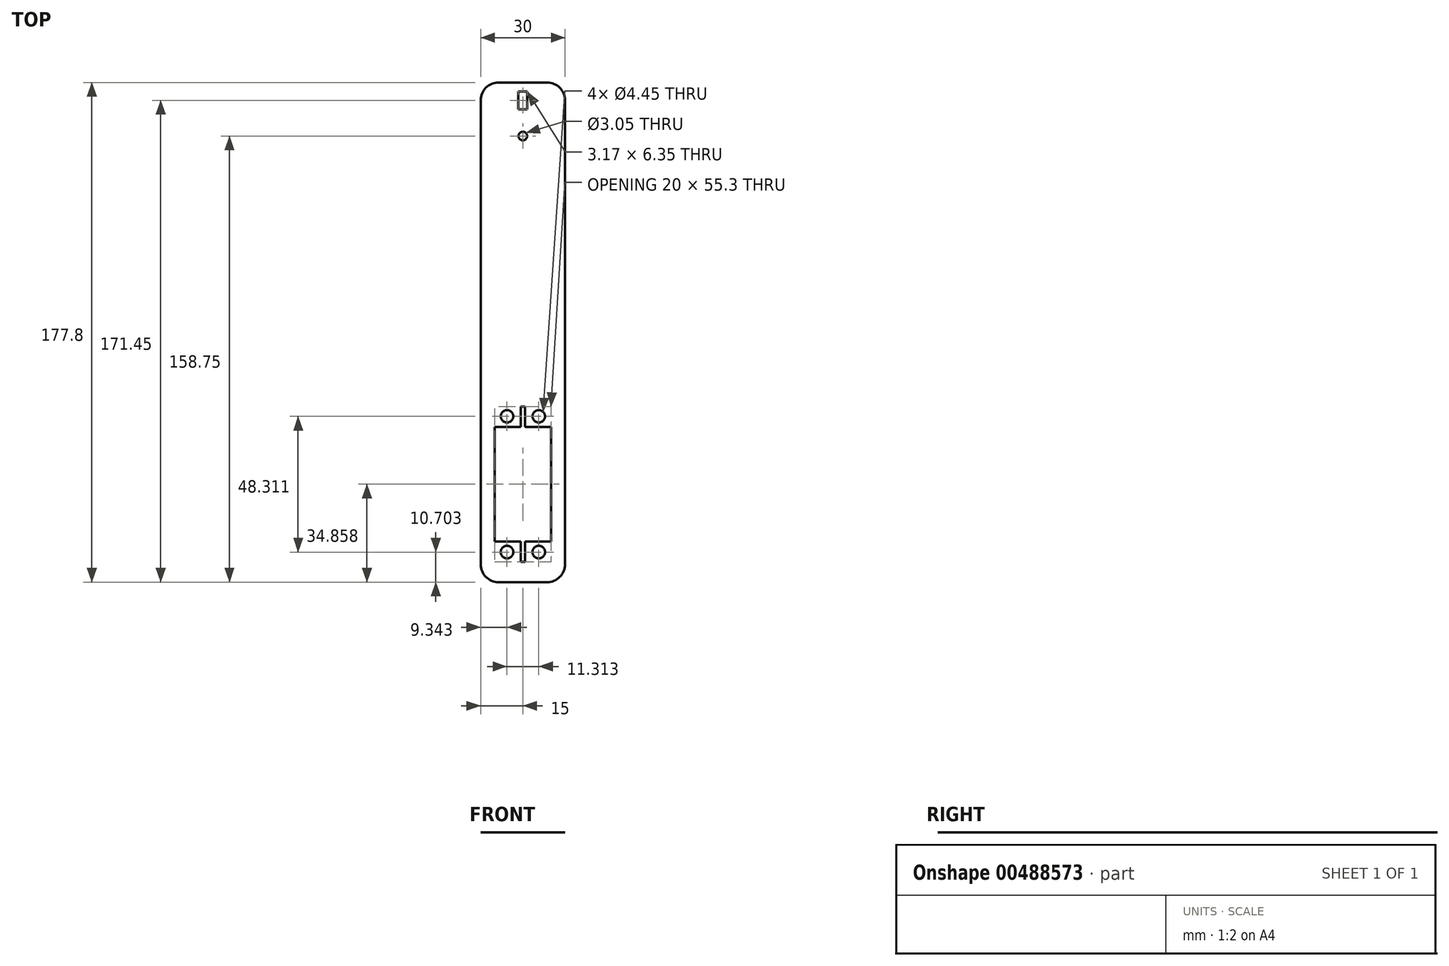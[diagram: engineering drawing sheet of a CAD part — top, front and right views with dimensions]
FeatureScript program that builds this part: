
annotation { "Feature Type Name" : "Feature", "Feature Type Description" : "" }
export const myFeature = defineFeature(function(context is Context, id is Id, definition is map)
    precondition{}
    {
        {
            var Q0;
            Q0=qCreatedBy(makeId("Top.planeOp"),FACE);
            var sketch = newSketch(context, id + "F0", { "sketchPlane" : qUnion([Q0])});
            skLineSegment(sketch, "E0.bottom", {"start": v(8.65, 88.9) * mm, "end": v(-8.65, 88.9) * mm});
            skLineSegment(sketch, "E0.top", {"start": v(8.65, -88.9) * mm, "end": v(-8.65, -88.9) * mm});
            skLineSegment(sketch, "E0.left", {"start": v(15, 82.55) * mm, "end": v(15, -82.55) * mm});
            skLineSegment(sketch, "E0.right", {"start": v(-15, 82.55) * mm, "end": v(-15, -82.55) * mm});
            skPoint(sketch, "E0.middle", {"position": v(0, 0) * mm});
            skLineSegment(sketch, "E1.bottom", {"start": v(10, -33.7) * mm, "end": v(0.75, -33.7) * mm});
            skLineSegment(sketch, "E1.top", {"start": v(10, -74.39) * mm, "end": v(0.75, -74.39) * mm});
            skLineSegment(sketch, "E1.left", {"start": v(10, -33.7) * mm, "end": v(10, -74.39) * mm});
            skLineSegment(sketch, "E1.right", {"start": v(-10, -33.7) * mm, "end": v(-10, -74.39) * mm});
            skPoint(sketch, "E1.middle", {"position": v(0, -54.04) * mm});
            skLineSegment(sketch, "E2.bottom", {"start": v(1.59, 79.38) * mm, "end": v(-1.59, 79.38) * mm});
            skLineSegment(sketch, "E2.top", {"start": v(1.59, 85.73) * mm, "end": v(-1.59, 85.73) * mm});
            skLineSegment(sketch, "E2.left", {"start": v(1.59, 79.38) * mm, "end": v(1.59, 85.73) * mm});
            skLineSegment(sketch, "E2.right", {"start": v(-1.59, 79.38) * mm, "end": v(-1.59, 85.73) * mm});
            skPoint(sketch, "E2.middle", {"position": v(0, 82.55) * mm});
            skCircle(sketch, "E3", {"center": v(5.66, -29.89) * mm, "radius": 2.22 * mm});
            skCircle(sketch, "E4", {"center": v(-5.66, -29.89) * mm, "radius": 2.22 * mm});
            skCircle(sketch, "E5", {"center": v(5.66, -78.2) * mm, "radius": 2.22 * mm});
            skCircle(sketch, "E6", {"center": v(-5.66, -78.2) * mm, "radius": 2.22 * mm});
            skLineSegment(sketch, "E7.top", {"start": v(-0.75, -26.4) * mm, "end": v(0.75, -26.4) * mm});
            skLineSegment(sketch, "E7.left", {"start": v(-0.75, -33.7) * mm, "end": v(-0.75, -26.4) * mm});
            skLineSegment(sketch, "E7.right", {"start": v(0.75, -33.7) * mm, "end": v(0.75, -26.4) * mm});
            skLineSegment(sketch, "E8.top", {"start": v(-0.75, -81.7) * mm, "end": v(0.75, -81.7) * mm});
            skLineSegment(sketch, "E8.left", {"start": v(-0.75, -74.39) * mm, "end": v(-0.75, -81.7) * mm});
            skLineSegment(sketch, "E8.right", {"start": v(0.75, -74.39) * mm, "end": v(0.75, -81.7) * mm});
            skLineSegment(sketch, "E9.trimOffspring", {"start": v(-0.75, -33.7) * mm, "end": v(-10, -33.7) * mm});
            skLineSegment(sketch, "E10.trimOffspring", {"start": v(-0.75, -74.39) * mm, "end": v(-10, -74.39) * mm});
            skCircle(sketch, "E11", {"center": v(0, 69.85) * mm, "radius": 1.52 * mm});
            skPoint(sketch, "E12.visualSharp", {"position": v(-15, 88.9) * mm});
            skArc(sketch, "E12.filletArc", {"start": v(-8.65, 88.9) * mm, "mid": v(-13.14, 87.04) * mm, "end": v(-15, 82.55) * mm});
            skPoint(sketch, "E13.visualSharp", {"position": v(15, 88.9) * mm});
            skArc(sketch, "E13.filletArc", {"start": v(15, 82.55) * mm, "mid": v(13.14, 87.04) * mm, "end": v(8.65, 88.9) * mm});
            skPoint(sketch, "E14.visualSharp", {"position": v(-15, -88.9) * mm});
            skArc(sketch, "E14.filletArc", {"start": v(-15, -82.55) * mm, "mid": v(-13.14, -87.04) * mm, "end": v(-8.65, -88.9) * mm});
            skPoint(sketch, "E15.visualSharp", {"position": v(15, -88.9) * mm});
            skArc(sketch, "E15.filletArc", {"start": v(8.65, -88.9) * mm, "mid": v(13.14, -87.04) * mm, "end": v(15, -82.55) * mm});
            skSolve(sketch);
        }
        {
            var Q0;
            Q0=makeQuery(id+"F0.imprint","IMPRINT",FACE,{"disambiguationData":[TD([[makeQuery(id+"F0.imprint","IMPRINT",EDGE,{"derivedFrom":sQuery(id+"F0.wireOp",EDGE,"E0.bottom")}),1.0]])]});
            extrude(context, id + "F1", {"entities" : qUnion([Q0]), "depth" : 1 / 203.2 * mm});
        }
    });
